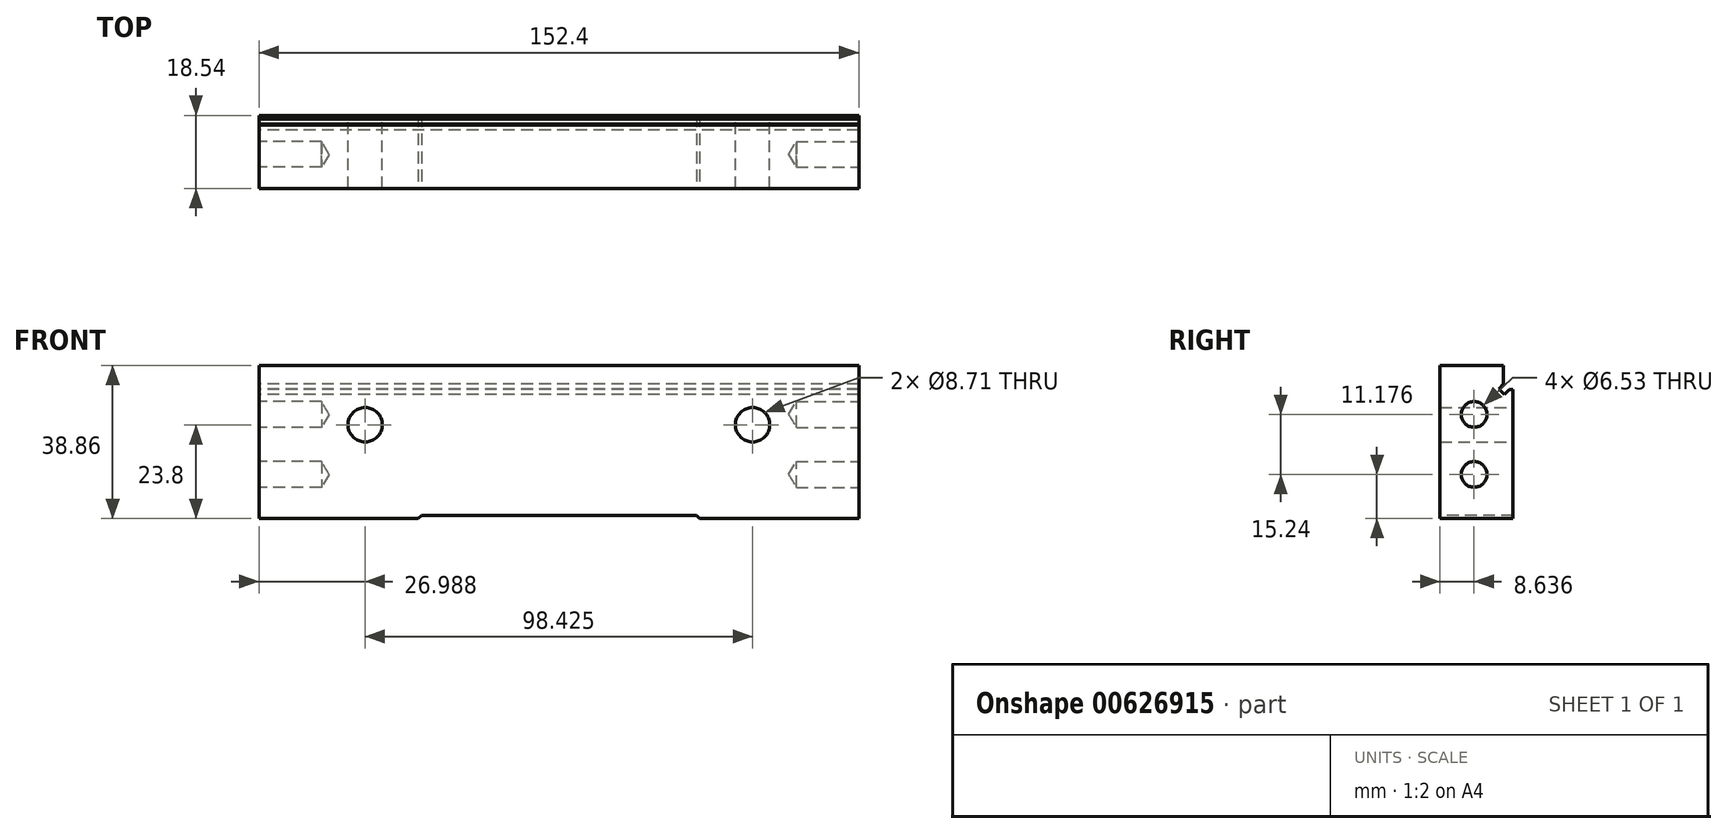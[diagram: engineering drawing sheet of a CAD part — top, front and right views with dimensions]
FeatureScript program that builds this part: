
annotation { "Feature Type Name" : "Feature", "Feature Type Description" : "" }
export const myFeature = defineFeature(function(context is Context, id is Id, definition is map)
    precondition{}
    {
        {
            var Q0;
            Q0=qCreatedBy(makeId("Right.planeOp"),FACE);
            var sketch = newSketch(context, id + "F0", { "sketchPlane" : qUnion([Q0])});
            skLineSegment(sketch, "E0", {"start": v(0, 0) * mm, "end": v(0, 38.86) * mm});
            skLineSegment(sketch, "E1", {"start": v(0, 38.86) * mm, "end": v(16.13, 38.86) * mm});
            skLineSegment(sketch, "E2", {"start": v(16.13, 38.86) * mm, "end": v(16.13, 34.2) * mm});
            skLineSegment(sketch, "E3", {"start": v(17.57, 32.77) * mm, "end": v(18.54, 32.77) * mm});
            skLineSegment(sketch, "E4", {"start": v(18.54, 32.77) * mm, "end": v(18.54, 0) * mm});
            skLineSegment(sketch, "E5", {"start": v(18.54, 0) * mm, "end": v(0, 0) * mm});
            skLineSegment(sketch, "E6", {"start": v(16.13, 34.2) * mm, "end": v(14.87, 32.95) * mm});
            skLineSegment(sketch, "E7", {"start": v(14.87, 32.95) * mm, "end": v(16.3, 31.5) * mm});
            skLineSegment(sketch, "E8", {"start": v(16.3, 31.5) * mm, "end": v(17.57, 32.77) * mm});
            skPoint(sketch, "E9.orphan", {"position": v(16.13, 32.77) * mm});
            skSolve(sketch);
        }
        {
            var Q0;
            Q0 = qSketchRegion(id + "F0", true);
            extrude(context, id + "F1", {"entities" : qUnion([Q0]), "depth" : 76.2 * mm, "offsetDistance" : 25.4 * mm, "hasSecondDirection" : true, "secondDirectionOppositeDirection" : true, "secondDirectionDepth" : 76.2 * mm});
        }
        {
            var Q0;
            Q0=makeQuery(id+"F1.opExtrude","CAP_FACE",FACE,{"disambiguationData":[OSD([sQuery(id+"F0.wireOp",EDGE,"E0"),sQuery(id+"F0.wireOp",EDGE,"E1"),sQuery(id+"F0.wireOp",EDGE,"E2"),sQuery(id+"F0.wireOp",EDGE,"E3"),sQuery(id+"F0.wireOp",EDGE,"E4"),sQuery(id+"F0.wireOp",EDGE,"E5"),sQuery(id+"F0.wireOp",EDGE,"E6"),sQuery(id+"F0.wireOp",EDGE,"E7"),sQuery(id+"F0.wireOp",EDGE,"E8")])],"isStart":false});
            var sketch = newSketch(context, id + "F2", { "sketchPlane" : qUnion([Q0])});
            skCircle(sketch, "E10", {"center": v(8.64, 26.42) * mm, "radius": 3.97 * mm});
            skCircle(sketch, "E11", {"center": v(8.64, 11.18) * mm, "radius": 3.97 * mm});
            skSolve(sketch);
        }
        {
            var Q0;
            Q0=sQuery(id+"F2.wireOp",VERTEX,"E11.center");
            var Q1;
            Q1=sQuery(id+"F2.wireOp",VERTEX,"E10.center");
            var Q2;
            Q2=makeQuery(id+"F1.opExtrude","SWEPT_BODY",BODY,{"disambiguationData":[OSD([sQuery(id+"F0.wireOp",EDGE,"E0"),sQuery(id+"F0.wireOp",EDGE,"E1"),sQuery(id+"F0.wireOp",EDGE,"E2"),sQuery(id+"F0.wireOp",EDGE,"E3"),sQuery(id+"F0.wireOp",EDGE,"E4"),sQuery(id+"F0.wireOp",EDGE,"E5"),sQuery(id+"F0.wireOp",EDGE,"E6"),sQuery(id+"F0.wireOp",EDGE,"E7"),sQuery(id+"F0.wireOp",EDGE,"E8")])]});
            hole(context, id + "F3", {"style" : HoleStyle.SIMPLE, "endStyle" : HoleEndStyle.BLIND, "standardTappedOrClearance" : lookupTablePath({ "standard" : "ANSI", "engagement" : "75%", "pitch" : "18 tpi", "size" : "5/16", "type" : "Tapped" }), "standardBlindInLast" : lookupTablePath({ "standard" : "ANSI", "engagement" : "75%", "pitch" : "18 tpi", "size" : "5/16", "type" : "Tapped" }), "holeDiameter" : 6.53 * mm, "majorDiameter" : 7.94 * mm, "showTappedDepth" : true, "holeDepth" : 15.88 * mm, "isTappedThrough" : true, "tappedDepth" : 11.64 * mm, "tapClearance" : 3, "locations" : qUnion([Q0, Q1]), "scope" : qUnion([Q2])});
        }
        {
            var Q0;
            Q0=makeQuery(id+"F1.opExtrude","CAP_FACE",FACE,{"disambiguationData":[OSD([sQuery(id+"F0.wireOp",EDGE,"E0"),sQuery(id+"F0.wireOp",EDGE,"E1"),sQuery(id+"F0.wireOp",EDGE,"E2"),sQuery(id+"F0.wireOp",EDGE,"E3"),sQuery(id+"F0.wireOp",EDGE,"E4"),sQuery(id+"F0.wireOp",EDGE,"E5"),sQuery(id+"F0.wireOp",EDGE,"E6"),sQuery(id+"F0.wireOp",EDGE,"E7"),sQuery(id+"F0.wireOp",EDGE,"E8")])],"isStart":true});
            var sketch = newSketch(context, id + "F4", { "sketchPlane" : qUnion([Q0])});
            skCircle(sketch, "E12.0", {"center": v(-8.64, 11.18) * mm, "radius": 3.26 * mm});
            skCircle(sketch, "E13.0", {"center": v(-8.64, 26.42) * mm, "radius": 3.26 * mm});
            skSolve(sketch);
        }
        {
            var Q0;
            Q0=sQuery(id+"F4.wireOp",VERTEX,"E13.0.center");
            var Q1;
            Q1=sQuery(id+"F4.wireOp",VERTEX,"E12.0.center");
            var Q2;
            Q2=makeQuery(id+"F1.opExtrude","SWEPT_BODY",BODY,{"disambiguationData":[OSD([sQuery(id+"F0.wireOp",EDGE,"E0"),sQuery(id+"F0.wireOp",EDGE,"E1"),sQuery(id+"F0.wireOp",EDGE,"E2"),sQuery(id+"F0.wireOp",EDGE,"E3"),sQuery(id+"F0.wireOp",EDGE,"E4"),sQuery(id+"F0.wireOp",EDGE,"E5"),sQuery(id+"F0.wireOp",EDGE,"E6"),sQuery(id+"F0.wireOp",EDGE,"E7"),sQuery(id+"F0.wireOp",EDGE,"E8")])]});
            hole(context, id + "F5", {"style" : HoleStyle.SIMPLE, "endStyle" : HoleEndStyle.BLIND, "standardTappedOrClearance" : lookupTablePath({ "standard" : "ANSI", "engagement" : "75%", "pitch" : "18 tpi", "size" : "5/16", "type" : "Tapped" }), "standardBlindInLast" : lookupTablePath({ "standard" : "ANSI", "engagement" : "75%", "pitch" : "18 tpi", "size" : "5/16", "type" : "Tapped" }), "holeDiameter" : 6.53 * mm, "majorDiameter" : 7.94 * mm, "showTappedDepth" : true, "holeDepth" : 15.88 * mm, "isTappedThrough" : true, "tappedDepth" : 11.64 * mm, "tapClearance" : 3, "locations" : qUnion([Q0, Q1]), "scope" : qUnion([Q2])});
        }
        {
            var Q0;
            Q0=makeQuery(id+"F1.opExtrude","SWEPT_FACE",FACE,{"disambiguationData":[OSD([sQuery(id+"F0.wireOp",EDGE,"E0")])]});
            var sketch = newSketch(context, id + "F6", { "sketchPlane" : qUnion([Q0])});
            skLineSegment(sketch, "E14", {"start": v(-35.73, 0) * mm, "end": v(-34.93, 0.8) * mm});
            skLineSegment(sketch, "E15", {"start": v(-34.93, 0.8) * mm, "end": v(34.93, 0.8) * mm});
            skLineSegment(sketch, "E16", {"start": v(34.93, 0.8) * mm, "end": v(35.73, 0) * mm});
            skLineSegment(sketch, "E17", {"start": v(-35.73, 0) * mm, "end": v(35.73, 0) * mm});
            skSolve(sketch);
        }
        {
            var Q0;
            Q0=makeQuery(id+"F6.imprint","IMPRINT",FACE,{"disambiguationData":[TD([[makeQuery(id+"F6.imprint","IMPRINT",EDGE,{"derivedFrom":sQuery(id+"F6.wireOp",EDGE,"E14")}),-1.0]])]});
            extrude(context, id + "F7", {"entities" : qUnion([Q0]), "operationType" : NewBodyOperationType.REMOVE, "endBound" : BoundingType.THROUGH_ALL, "oppositeDirection" : true, "depth" : 25.4 * mm, "offsetDistance" : 25.4 * mm});
        }
        {
            var Q0;
            Q0=makeQuery(id+"F1.opExtrude","SWEPT_FACE",FACE,{"disambiguationData":[OSD([sQuery(id+"F0.wireOp",EDGE,"E4")])]});
            var sketch = newSketch(context, id + "F8", { "sketchPlane" : qUnion([Q0])});
            skCircle(sketch, "E18", {"center": v(-49.21, 23.8) * mm, "radius": 4.36 * mm});
            skCircle(sketch, "E19", {"center": v(49.21, 23.8) * mm, "radius": 4.36 * mm});
            skSolve(sketch);
        }
        {
            var Q0;
            Q0 = qSketchRegion(id + "F8", true);
            extrude(context, id + "F9", {"entities" : qUnion([Q0]), "operationType" : NewBodyOperationType.REMOVE, "endBound" : BoundingType.THROUGH_ALL, "oppositeDirection" : true, "depth" : 25.4 * mm, "offsetDistance" : 25.4 * mm});
        }
    });
